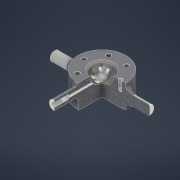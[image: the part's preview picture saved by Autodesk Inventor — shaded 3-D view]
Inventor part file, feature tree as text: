
AUTODESK INVENTOR PART (.ipt)
format: ipt  version: 2022 (Build 260153000, 153)  size: 267,776 bytes
history: native  units: mm
features: sketch x7, chamfer x4, extrude x3, other x2, revolve x2, hole x2, thread x1, mirror x1, pattern_circular x1
ambient origin geometry x8: Origin, YZ Plane, XZ Plane, XY Plane, X Axis, Y Axis, Z Axis, Center Point
bodies: Body1 (feature_tree)
feature tree (23):
  extrude  "Выдавливание8"  Depth=100.0mm
  other  "РабПлоскость16"
  revolve  "Вращение8"
  chamfer  "Фаска8"  Distance=50.0mm
  thread  "Резьба4"
  chamfer  "Фаска9"  Distance=100.0mm
  mirror  "Зеркальное отражение4"
  revolve  "Вращение9"
  other  "РабПлоскость17"
  extrude  "Выдавливание9"  Depth=10.0mm
  chamfer  "Фаска10"  Distance=35.0mm
  hole  "Отверстие6"  [1 undecoded]
  extrude  "Выдавливание10"  TaperAngle=360.0deg  [1 undecoded]
  hole  "Отверстие7"  [1 undecoded]
  pattern_circular  "Круговой массив4"  [2 undecoded]
  chamfer  "Фаска11"  Distance=2.0mm Angle=45.0deg
  sketch  "Эскиз23"
  sketch  "Эскиз25"
  sketch  "Эскиз26"
  sketch  "Эскиз29"
  sketch  "Эскиз30"
  sketch  "Эскиз31"
  sketch  "Эскиз32"
note: 5 required parameter values undecoded (feature->parameter linkage not recoverable at this tier; creation-order binding heuristic only, values carry confidence <= 0.55)
